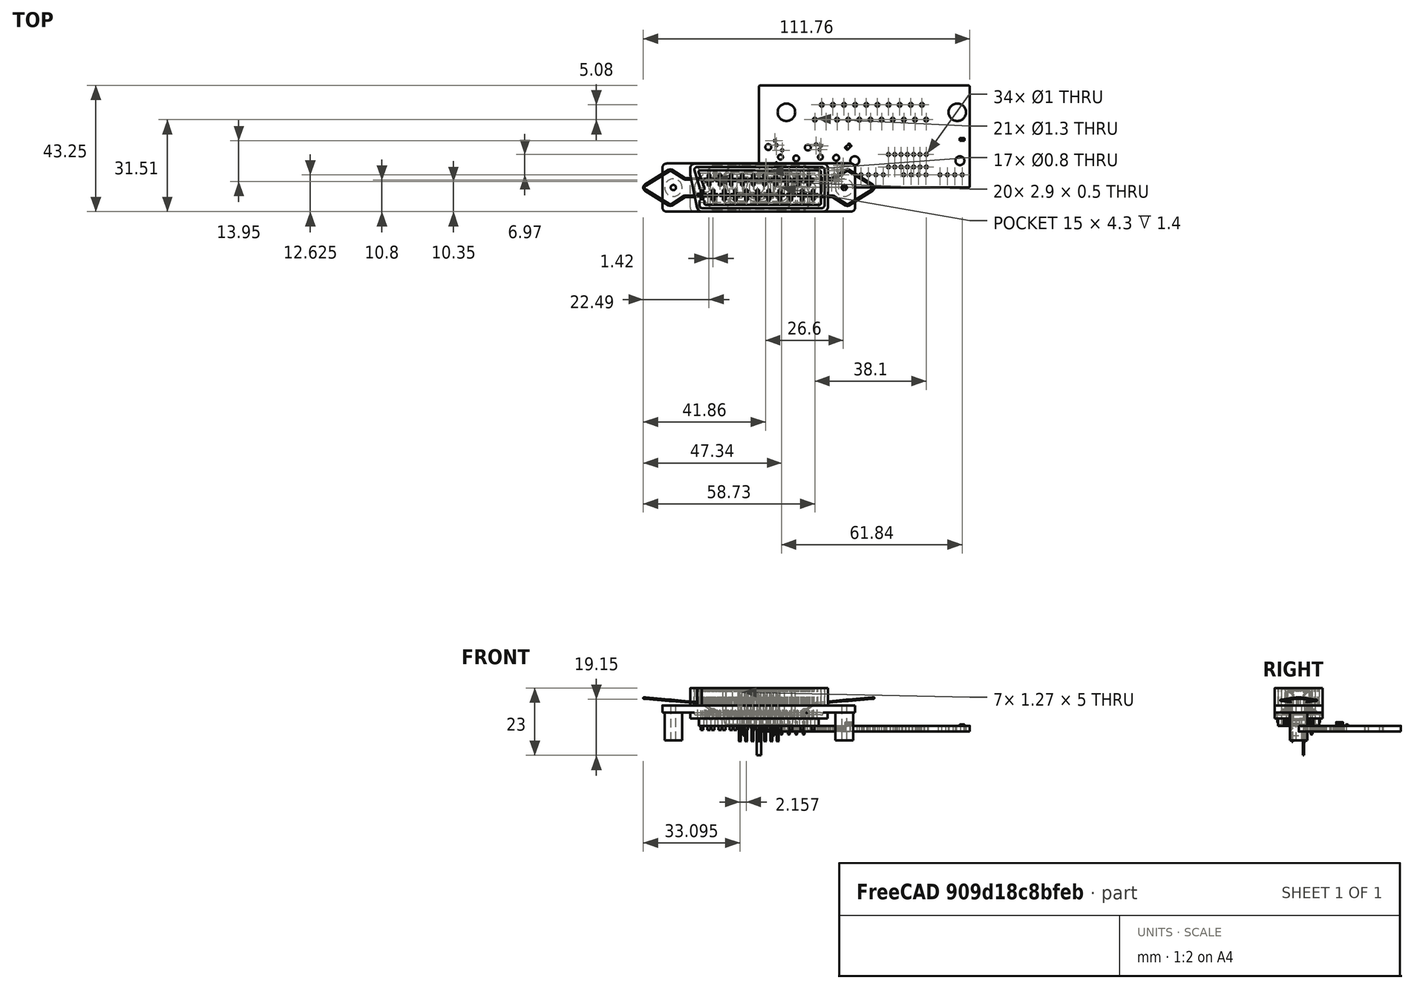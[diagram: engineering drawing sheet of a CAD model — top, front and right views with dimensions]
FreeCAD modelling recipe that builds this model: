
FCSTD DOCUMENT  (FreeCAD 0.20R29177 (Git))
Label: Ultra-AV
License: All rights reserved
LicenseURL: http://en.wikipedia.org/wiki/All_rights_reserved
objects: Part::Feature×44, App::Part×14, App::Link×9, PartDesign::AdditiveBox×8, PartDesign::AdditiveCylinder×6, PartDesign::SubtractiveCylinder×4, PartDesign::Body×4, PartDesign::Fillet×4, Sketcher::SketchObject×3, PartDesign::CoordinateSystem×1
note: 96 computed .brp shape members not serialized (recipe doc carries the construction recipe); baked Part::Feature solids carry a one-line shape summary decoded from their .brp

FEATURE [PartDesign::CoordinateSystem] Local_CS_ecc4
  AttacherType = Attacher::AttachEngine3D
FEATURE [Part::Feature] Pcb_ecc4
  Placement = pos=(-111.2,111.3,0) rot=(0,0,1;0rad)
  shape: bbox 72.2 x 35 x 2 mm, 96 faces (baked)
FEATURE [Sketcher::SketchObject] PCB_Sketch_ecc4
  FullyConstrained = false
  sketch-geometry (29):
    g0: LineSegment StartX=0.5 StartY=35 StartZ=0 EndX=71.7 EndY=35 EndZ=0
    g1: LineSegment StartX=0.001685 StartY=7.99999 StartZ=0 EndX=3e-16 EndY=34.5 EndZ=0
    g2: LineSegment StartX=72.2 StartY=34.5 StartZ=0 EndX=72.2 EndY=0.5 EndZ=0
    g3: LineSegment StartX=71.7 StartY=2.8e-15 StartZ=0 EndX=8.00168 EndY=-7e-06 EndZ=0
    g4: ArcOfCircle CenterX=8.00169 CenterY=7.99999 CenterZ=0 NormalX=0 NormalY=0 NormalZ=-1 AngleXU=-1.5708 Radius=8 StartAngle=0 EndAngle=1.5708
    g5: ArcOfCircle CenterX=0.500001 CenterY=34.5 CenterZ=0 NormalX=0 NormalY=0 NormalZ=-1 AngleXU=2.66714e-06 Radius=0.500001 StartAngle=0 EndAngle=1.57079
    g6: ArcOfCircle CenterX=71.7 CenterY=34.5 CenterZ=0 NormalX=0 NormalY=0 NormalZ=-1 AngleXU=1.5708 Radius=0.500001 StartAngle=0 EndAngle=1.57079
    g7: ArcOfCircle CenterX=71.7 CenterY=0.500001 CenterZ=0 NormalX=0 NormalY=0 NormalZ=-1 AngleXU=-3.14159 Radius=0.500001 StartAngle=0 EndAngle=1.57079
    g8: Circle CenterX=26.9 CenterY=5.8 CenterZ=0 NormalX=0 NormalY=0 NormalZ=1 AngleXU=0 Radius=0.4
    g9: Circle CenterX=28.9 CenterY=7.6 CenterZ=0 NormalX=0 NormalY=0 NormalZ=1 AngleXU=0 Radius=0.4
    g10: Circle CenterX=11.8 CenterY=2.95 CenterZ=0 NormalX=0 NormalY=0 NormalZ=1 AngleXU=0 Radius=0.25
    g11: Circle CenterX=19.6 CenterY=14.8 CenterZ=0 NormalX=0 NormalY=0 NormalZ=1 AngleXU=0 Radius=0.4
    g12: Circle CenterX=6 CenterY=8.4 CenterZ=0 NormalX=0 NormalY=0 NormalZ=1 AngleXU=0 Radius=0.25
    g13: Circle CenterX=6.05 CenterY=14.55 CenterZ=0 NormalX=0 NormalY=0 NormalZ=1 AngleXU=0 Radius=0.4
    g14: Circle CenterX=23.5 CenterY=2.1 CenterZ=0 NormalX=0 NormalY=0 NormalZ=1 AngleXU=0 Radius=0.4
    g15: Circle CenterX=28.2 CenterY=6.3 CenterZ=0 NormalX=0 NormalY=0 NormalZ=1 AngleXU=0 Radius=0.4
    g16: Circle CenterX=22.2 CenterY=2.1 CenterZ=0 NormalX=0 NormalY=0 NormalZ=1 AngleXU=0 Radius=0.4
    g17: Circle CenterX=2.5 CenterY=7.4 CenterZ=0 NormalX=0 NormalY=0 NormalZ=1 AngleXU=0 Radius=0.4
    g18: Circle CenterX=3.1 CenterY=5 CenterZ=0 NormalX=0 NormalY=0 NormalZ=1 AngleXU=0 Radius=0.4
    g19: Circle CenterX=27.4 CenterY=2.8 CenterZ=0 NormalX=0 NormalY=0 NormalZ=1 AngleXU=0 Radius=0.4
    g20: Circle CenterX=20.8 CenterY=13 CenterZ=0 NormalX=0 NormalY=0 NormalZ=1 AngleXU=0 Radius=0.4
    g21: Circle CenterX=21.2 CenterY=14.3 CenterZ=0 NormalX=0 NormalY=0 NormalZ=1 AngleXU=0 Radius=0.4
    g22: Circle CenterX=4.55 CenterY=6 CenterZ=0 NormalX=0 NormalY=0 NormalZ=1 AngleXU=0 Radius=0.25
    g23: Circle CenterX=8 CenterY=12.8 CenterZ=0 NormalX=0 NormalY=0 NormalZ=1 AngleXU=0 Radius=0.4
    g24: Circle CenterX=10.9 CenterY=2.75 CenterZ=0 NormalX=0 NormalY=0 NormalZ=1 AngleXU=0 Radius=0.25
    g25: Circle CenterX=26.3 CenterY=2.1 CenterZ=0 NormalX=0 NormalY=0 NormalZ=1 AngleXU=0 Radius=0.4
    g26: Circle CenterX=24.9 CenterY=2.1 CenterZ=0 NormalX=0 NormalY=0 NormalZ=1 AngleXU=0 Radius=0.4
    g27: Circle CenterX=5.55 CenterY=16.05 CenterZ=0 NormalX=0 NormalY=0 NormalZ=1 AngleXU=0 Radius=0.4
    g28: Circle CenterX=2.3 CenterY=6.1 CenterZ=0 NormalX=0 NormalY=0 NormalZ=1 AngleXU=0 Radius=0.4
  constraints (8):
    c: Coincident(g1,g4)
    c: Coincident(g1,g5)
    c: Coincident(g0,g5)
    c: Coincident(g3,g4)
    c: Coincident(g3,g7)
    c: Coincident(g0,g6)
    c: Coincident(g2,g7)
    c: Coincident(g2,g6)
FEATURE [App::Part] Board_Geoms_ecc4
  Group = -> [Local_CS_ecc4,Pcb_ecc4,PCB_Sketch_ecc4]
  Origin = -> Origin
FEATURE [Part::Feature] Shape  label="R12_R_0603_1608Metric_fea975d0d3e0"
  Placement = pos=(69.6,16.5,0) rot=(0,0,1;0rad)
  shape: bbox 1.6 x 0.8 x 0.45 mm, 26 faces (baked)
FEATURE [Part::Feature] Shape001  label="J5_PinHeader_1x04_P254mm_Horizontal_92fba9bb2b89"
  Placement = pos=(15.4,4.4,0) rot=(0,0,-1;1.5708rad)
  shape: bbox 10.16 x 10.36 x 5.54 mm, 112 faces (baked)
FEATURE [App::Link] R12_R_0603_1608Metric_fea975d0d3e0_ln_  label="R16_R_0603_1608Metric_98c7d70c461d"
  LinkPlacement = pos=(70.45,14.175,0) rot=(0,0,-1;0.785398rad)
  LinkedObject = -> Shape
  Placement = pos=(70.45,14.175,0) rot=(0,0,-1;0.785398rad)
FEATURE [Part::Feature] Part__Feature  label="Plastic-insert"
  Placement = pos=(0,0,0.05) rot=(0,0,1;0rad)
  shape: bbox 22.57 x 11.5 x 12.3 mm, 343 faces (baked)
FEATURE [Part::Feature] Part__Feature001  label="chassis-metal"
  Placement = pos=(0,0,4.5) rot=(0,0,1;0rad)
  shape: bbox 43.9 x 15.3 x 12.3 mm, 159 faces (baked)
FEATURE [Part::Feature] Part__Feature002  label="base-pin"
  Placement = pos=(-6.48,0,4.5) rot=(0,0,1;0rad)
  shape: bbox 1.5 x 1.495 x 17.96 mm, 46 faces (baked)
FEATURE [Part::Feature] Part__Feature003  label="base-pin001"
  Placement = pos=(-4.32,0,4.5) rot=(0,0,1;0rad)
  shape: bbox 1.5 x 1.495 x 17.96 mm, 46 faces (baked)
FEATURE [Part::Feature] Part__Feature004  label="base-pin002"
  Placement = pos=(-2.16,0,4.5) rot=(0,0,1;0rad)
  shape: bbox 1.5 x 1.495 x 17.96 mm, 46 faces (baked)
FEATURE [Part::Feature] Part__Feature005  label="base-pin003"
  Placement = pos=(0,0,4.5) rot=(0,0,1;0rad)
  shape: bbox 1.5 x 1.495 x 17.96 mm, 46 faces (baked)
FEATURE [Part::Feature] Part__Feature006  label="base-pin004"
  Placement = pos=(2.16,0,4.5) rot=(0,0,1;0rad)
  shape: bbox 1.5 x 1.495 x 17.96 mm, 46 faces (baked)
FEATURE [Part::Feature] Part__Feature007  label="base-pin005"
  Placement = pos=(4.32,0,4.5) rot=(0,0,1;0rad)
  shape: bbox 1.5 x 1.495 x 17.96 mm, 46 faces (baked)
FEATURE [Part::Feature] Part__Feature008  label="base-pin006"
  Placement = pos=(6.48,0,4.5) rot=(0,0,1;0rad)
  shape: bbox 1.5 x 1.495 x 17.96 mm, 46 faces (baked)
FEATURE [App::Part] pins_top  label="pins-top"
  Group = -> [Part__Feature002,Part__Feature003,Part__Feature004,Part__Feature005,Part__Feature006,Part__Feature007,Part__Feature008]
  Origin = -> Origin008
FEATURE [Part::Feature] Part__Feature009  label="pins-bot"
  Placement = pos=(0,0,0) rot=(0,0,1;3.14159rad)
  shape: bbox 1.5 x 1.495 x 17.96 mm, 46 faces (baked)
FEATURE [Part::Feature] Part__Feature010  label="pins-bot001"
  Placement = pos=(0,0,0) rot=(0,0,1;3.14159rad)
  shape: bbox 1.5 x 1.495 x 17.96 mm, 46 faces (baked)
FEATURE [Part::Feature] Part__Feature011  label="pins-bot002"
  Placement = pos=(0,0,0) rot=(0,0,1;3.14159rad)
  shape: bbox 1.5 x 1.495 x 17.96 mm, 46 faces (baked)
FEATURE [Part::Feature] Part__Feature012  label="pins-bot003"
  Placement = pos=(0,0,0) rot=(0,0,1;3.14159rad)
  shape: bbox 1.5 x 1.495 x 17.96 mm, 46 faces (baked)
FEATURE [Part::Feature] Part__Feature013  label="pins-bot004"
  Placement = pos=(0,0,0) rot=(0,0,1;3.14159rad)
  shape: bbox 1.5 x 1.495 x 17.96 mm, 46 faces (baked)
FEATURE [Part::Feature] Part__Feature014  label="pins-bot005"
  Placement = pos=(0,0,0) rot=(0,0,1;3.14159rad)
  shape: bbox 1.5 x 1.495 x 17.96 mm, 46 faces (baked)
FEATURE [Part::Feature] Part__Feature015  label="pins-bot006"
  Placement = pos=(0,0,0) rot=(0,0,1;3.14159rad)
  shape: bbox 1.5 x 1.495 x 17.96 mm, 46 faces (baked)
FEATURE [App::Part] pins_bot  label="pins-bot007"
  Group = -> [Part__Feature009,Part__Feature010,Part__Feature011,Part__Feature012,Part__Feature013,Part__Feature014,Part__Feature015]
  Origin = -> Origin009
FEATURE [Part::Feature] Part__Feature017  label="Handle Left"
  shape: bbox 24.46 x 12.5 x 5.12 mm, 52 faces (baked)
FEATURE [Part::Feature] Part__Feature018  label="Handle Right"
  Placement = pos=(0,0,0) rot=(0,0,1;3.14159rad)
  shape: bbox 24.46 x 12.5 x 5.12 mm, 52 faces (baked)
FEATURE [App::Part] Handles
  Group = -> [Part__Feature017,Part__Feature018]
  Origin = -> Origin010
FEATURE [App::Part] Norcomp_111_014_213L001  label="J9_Norcomp_111_014_213L001_9b66603eb921"
  Group = -> [Part__Feature,Part__Feature001,pins_top,pins_bot,Handles]
  Origin = -> Origin011
  Placement = pos=(50.85,9.2,0) rot=(0,0,1;0rad)
FEATURE [App::Link] J5_PinHeader_1x04_P254mm_Horizontal_92fba9bb2b89_ln_  label="J3_PinHeader_1x04_P254mm_Horizontal_ad84bd842bec"
  LinkPlacement = pos=(28.4,4.4,0) rot=(0,0,-1;1.5708rad)
  LinkedObject = -> Shape001
  Placement = pos=(28.4,4.4,0) rot=(0,0,-1;1.5708rad)
FEATURE [App::Link] R12_R_0603_1608Metric_fea975d0d3e0_ln_001  label="R100_R_0603_1608Metric_c06db4a17feb"
  LinkPlacement = pos=(29.3664,15.2664,0) rot=(0,0,1;3.92699rad)
  LinkedObject = -> Shape
  Placement = pos=(29.3664,15.2664,0) rot=(0,0,1;3.92699rad)
FEATURE [Part::Feature] Part__Feature019  label="Plastic-body"
  Placement = pos=(0,0,7) rot=(0,0,1;0rad)
  shape: bbox 66 x 16.5 x 17.9 mm, 446 faces (baked)
FEATURE [Part::Feature] Part__Feature020  label="pin-top"
  Placement = pos=(2.38,5.0875,0) rot=(0,0,1;0rad)
  shape: bbox 2.8 x 0.4 x 14.4 mm, 20 faces (baked)
FEATURE [Part::Feature] Part__Feature021  label="pin-top001"
  Placement = pos=(6.18,5.0875,0) rot=(0,0,1;0rad)
  shape: bbox 2.8 x 0.4 x 14.4 mm, 20 faces (baked)
FEATURE [Part::Feature] Part__Feature022  label="pin-top002"
  Placement = pos=(9.98,5.0875,0) rot=(0,0,1;0rad)
  shape: bbox 2.8 x 0.4 x 14.4 mm, 20 faces (baked)
FEATURE [Part::Feature] Part__Feature023  label="pin-top003"
  Placement = pos=(13.78,5.0875,0) rot=(0,0,1;0rad)
  shape: bbox 2.8 x 0.4 x 14.4 mm, 20 faces (baked)
FEATURE [Part::Feature] Part__Feature024  label="pin-top004"
  Placement = pos=(17.58,5.0875,0) rot=(0,0,1;0rad)
  shape: bbox 2.8 x 0.4 x 14.4 mm, 20 faces (baked)
FEATURE [Part::Feature] Part__Feature025  label="pin-top005"
  Placement = pos=(21.38,5.0875,0) rot=(0,0,1;0rad)
  shape: bbox 2.8 x 0.4 x 14.4 mm, 20 faces (baked)
FEATURE [Part::Feature] Part__Feature026  label="pin-top006"
  Placement = pos=(25.18,5.0875,0) rot=(0,0,1;0rad)
  shape: bbox 2.8 x 0.4 x 14.4 mm, 20 faces (baked)
FEATURE [Part::Feature] Part__Feature027  label="pin-top007"
  Placement = pos=(28.98,5.0875,0) rot=(0,0,1;0rad)
  shape: bbox 2.8 x 0.4 x 14.4 mm, 20 faces (baked)
FEATURE [Part::Feature] Part__Feature028  label="pin-top008"
  Placement = pos=(32.78,5.0875,0) rot=(0,0,1;0rad)
  shape: bbox 2.8 x 0.4 x 14.4 mm, 20 faces (baked)
FEATURE [Part::Feature] Part__Feature029  label="pin-top009"
  Placement = pos=(36.58,5.0875,0) rot=(0,0,1;0rad)
  shape: bbox 2.8 x 0.4 x 14.4 mm, 20 faces (baked)
FEATURE [App::Part] top_pins  label="top-pins"
  Group = -> [Part__Feature020,Part__Feature021,Part__Feature022,Part__Feature023,Part__Feature024,Part__Feature025,Part__Feature026,Part__Feature027,Part__Feature028,Part__Feature029]
  Origin = -> Origin012
FEATURE [Part::Feature] Part__Feature030  label="Pin-bot"
  shape: bbox 2.8 x 0.4 x 14.4 mm, 20 faces (baked)
FEATURE [Part::Feature] Part__Feature031  label="Pin-bot001"
  Placement = pos=(3.8,0,0) rot=(0,0,1;0rad)
  shape: bbox 2.8 x 0.4 x 14.4 mm, 20 faces (baked)
FEATURE [Part::Feature] Part__Feature032  label="Pin-bot002"
  Placement = pos=(7.6,0,0) rot=(0,0,1;0rad)
  shape: bbox 2.8 x 0.4 x 14.4 mm, 20 faces (baked)
FEATURE [Part::Feature] Part__Feature033  label="Pin-bot003"
  Placement = pos=(11.4,0,0) rot=(0,0,1;0rad)
  shape: bbox 2.8 x 0.4 x 14.4 mm, 20 faces (baked)
FEATURE [Part::Feature] Part__Feature034  label="Pin-bot004"
  Placement = pos=(15.2,0,0) rot=(0,0,1;0rad)
  shape: bbox 2.8 x 0.4 x 14.4 mm, 20 faces (baked)
FEATURE [Part::Feature] Part__Feature035  label="Pin-bot005"
  Placement = pos=(19,0,0) rot=(0,0,1;0rad)
  shape: bbox 2.8 x 0.4 x 14.4 mm, 20 faces (baked)
FEATURE [Part::Feature] Part__Feature036  label="Pin-bot006"
  Placement = pos=(22.8,0,0) rot=(0,0,1;0rad)
  shape: bbox 2.8 x 0.4 x 14.4 mm, 20 faces (baked)
FEATURE [Part::Feature] Part__Feature037  label="Pin-bot007"
  Placement = pos=(26.6,0,0) rot=(0,0,1;0rad)
  shape: bbox 2.8 x 0.4 x 14.4 mm, 20 faces (baked)
FEATURE [Part::Feature] Part__Feature038  label="Pin-bot008"
  Placement = pos=(30.4,0,0) rot=(0,0,1;0rad)
  shape: bbox 2.8 x 0.4 x 14.4 mm, 20 faces (baked)
FEATURE [Part::Feature] Part__Feature039  label="Pin-bot009"
  Placement = pos=(34.2,0,0) rot=(0,0,1;0rad)
  shape: bbox 2.8 x 0.4 x 14.4 mm, 20 faces (baked)
FEATURE [Part::Feature] Part__Feature040  label="Pin-bot010"
  Placement = pos=(38,0,0) rot=(0,0,1;0rad)
  shape: bbox 2.8 x 0.4 x 14.4 mm, 20 faces (baked)
FEATURE [App::Part] Array001
  Group = -> [Part__Feature030,Part__Feature031,Part__Feature032,Part__Feature033,Part__Feature034,Part__Feature035,Part__Feature036,Part__Feature037,Part__Feature038,Part__Feature039,Part__Feature040]
  Origin = -> Origin013
FEATURE [App::Part] TC_1578891_scart  label="J11_TC_1578891_scart_58c3af9e474b"
  Group = -> [Part__Feature019,top_pins,Array001]
  Origin = -> Origin014
  Placement = pos=(38.7,25.8,0) rot=(0,0,1;0rad)
FEATURE [Part::Feature] Shape002  label="C100_C_0805_2012Metric_50f9677266a3"
  Placement = pos=(30.6,14,0) rot=(0,0,1;0.785398rad)
  shape: bbox 2.298 x 2.298 x 1.25 mm, 28 faces (baked)
FEATURE [App::Link] R12_R_0603_1608Metric_fea975d0d3e0_ln_002  label="R17_R_0603_1608Metric_099708a927e8"
  LinkPlacement = pos=(32.6166,2.78336,0) rot=(0,0,-1;0.785398rad)
  LinkedObject = -> Shape
  Placement = pos=(32.6166,2.78336,0) rot=(0,0,-1;0.785398rad)
FEATURE [App::Link] J5_PinHeader_1x04_P254mm_Horizontal_92fba9bb2b89_ln_001  label="J1_PinHeader_1x04_P254mm_Horizontal_e9d8d5db6f15"
  LinkPlacement = pos=(62,4.375,-2) rot=(0.707107,-0.707107,0;3.14159rad)
  LinkedObject = -> Shape001
  Placement = pos=(62,4.375,-2) rot=(0.707107,-0.707107,0;3.14159rad)
FEATURE [App::Link] R12_R_0603_1608Metric_fea975d0d3e0_ln_003  label="R2_R_0603_1608Metric_0536453e6189"
  LinkPlacement = pos=(23.8,12.8,-2) rot=(0,1,0;3.14159rad)
  LinkedObject = -> Shape
  Placement = pos=(23.8,12.8,-2) rot=(0,1,0;3.14159rad)
FEATURE [App::Link] J5_PinHeader_1x04_P254mm_Horizontal_92fba9bb2b89_ln_002  label="J4_PinHeader_1x04_P254mm_Horizontal_ed954c910011"
  LinkPlacement = pos=(35,4.4,-2) rot=(0.707107,-0.707107,0;3.14159rad)
  LinkedObject = -> Shape001
  Placement = pos=(35,4.4,-2) rot=(0.707107,-0.707107,0;3.14159rad)
FEATURE [App::Link] R12_R_0603_1608Metric_fea975d0d3e0_ln_004  label="R1_R_0603_1608Metric_fdd1dcc8b35c"
  LinkPlacement = pos=(17.6334,10.3834,-2) rot=(0.92388,0.382683,0;3.14159rad)
  LinkedObject = -> Shape
  Placement = pos=(17.6334,10.3834,-2) rot=(0.92388,0.382683,0;3.14159rad)
FEATURE [App::Link] J5_PinHeader_1x04_P254mm_Horizontal_92fba9bb2b89_ln_003  label="J2_PinHeader_1x04_P254mm_Horizontal_2a461bf643cc"
  LinkPlacement = pos=(49.6,4.4,-2) rot=(0.707107,-0.707107,0;3.14159rad)
  LinkedObject = -> Shape001
  Placement = pos=(49.6,4.4,-2) rot=(0.707107,-0.707107,0;3.14159rad)
FEATURE [App::Part] Bot_ecc4
  Group = -> [J5_PinHeader_1x04_P254mm_Horizontal_92fba9bb2b89_ln_001,R12_R_0603_1608Metric_fea975d0d3e0_ln_003,J5_PinHeader_1x04_P254mm_Horizontal_92fba9bb2b89_ln_002,R12_R_0603_1608Metric_fea975d0d3e0_ln_004,J5_PinHeader_1x04_P254mm_Horizontal_92fba9bb2b89_ln_003]
  Origin = -> Origin004
FEATURE [PartDesign::AdditiveBox] Box
  AttacherType = Attacher::AttachEngine3D
  AttachmentOffset = pos=(-5.35,-3,0) rot=(0,0,1;0rad)
  Height = 0.4
  Length = 10.7
  MapMode = 5
  Placement = pos=(-5.35,-3,0) rot=(0,0,1;0rad)
  Support = -> [XY_Plane015]
  Width = 6
FEATURE [PartDesign::AdditiveCylinder] Cylinder
  Angle = 360
  AttacherType = Attacher::AttachEngine3D
  BaseFeature = -> Box
  FirstAngle = 0
  Height = 0.4
  MapMode = 5
  Radius = 5
  SecondAngle = 0
  Support = -> [XY_Plane015]
FEATURE [PartDesign::AdditiveCylinder] Cylinder001
  Angle = 360
  AttacherType = Attacher::AttachEngine3D
  BaseFeature = -> Cylinder
  FirstAngle = 0
  Height = 12
  MapMode = 5
  Radius = 4.15
  SecondAngle = 0
  Support = -> [XY_Plane015]
FEATURE [PartDesign::AdditiveCylinder] Cylinder003
  Angle = 360
  AttacherType = Attacher::AttachEngine3D
  AttachmentOffset = pos=(0,0,2) rot=(0,0,1;0rad)
  FirstAngle = 0
  Height = 10
  MapMode = 5
  Placement = pos=(0,0,2) rot=(0,0,1;0rad)
  Radius = 3.27
  SecondAngle = 0
  Support = -> [XY_Plane016]
FEATURE [PartDesign::SubtractiveCylinder] Cylinder004
  Angle = 360
  AttacherType = Attacher::AttachEngine3D
  AttachmentOffset = pos=(0,0,2) rot=(0,0,1;0rad)
  BaseFeature = -> Cylinder003
  FirstAngle = 0
  Height = 10
  MapMode = 5
  Placement = pos=(0,0,2) rot=(0,0,1;0rad)
  Radius = 1.75
  SecondAngle = 0
  Support = -> [XY_Plane016]
FEATURE [PartDesign::Body] Body001  label="Red inset"
  Group = -> [Cylinder003,Cylinder004]
  Origin = -> Origin016
  Tip = -> Cylinder004
FEATURE [PartDesign::Fillet] Fillet
  Base = -> Cylinder001 [Edge37]
  BaseFeature = -> Cylinder001
  Radius = 0.75
  SupportTransform = false
  UseAllEdges = false
FEATURE [PartDesign::SubtractiveCylinder] Cylinder002
  Angle = 360
  AttacherType = Attacher::AttachEngine3D
  AttachmentOffset = pos=(0,0,2) rot=(0,0,1;0rad)
  BaseFeature = -> Fillet
  FirstAngle = 0
  Height = 10
  MapMode = 5
  Placement = pos=(0,0,2) rot=(0,0,1;0rad)
  Radius = 3.3
  SecondAngle = 0
  Support = -> [XY_Plane015]
FEATURE [PartDesign::Fillet] Fillet001
  Base = -> Cylinder002 [Edge19]
  BaseFeature = -> Cylinder002
  Placement = pos=(0,0,2) rot=(0,0,1;0rad)
  Radius = 0.2
  SupportTransform = false
  UseAllEdges = false
FEATURE [PartDesign::AdditiveBox] Box001
  AttacherType = Attacher::AttachEngine3D
  AttachmentOffset = pos=(-0.75,1.4,-10.1) rot=(0,0,1;0rad)
  BaseFeature = -> Fillet001
  Height = 10.1
  Length = 1.5
  MapMode = 5
  Placement = pos=(-0.75,1.4,-10.1) rot=(0,0,1;0rad)
  Support = -> [XY_Plane015]
  Width = 0.4
FEATURE [PartDesign::AdditiveBox] Box002
  AttacherType = Attacher::AttachEngine3D
  AttachmentOffset = pos=(4.95,-3,-3.4) rot=(0,0,1;0rad)
  BaseFeature = -> Box001
  Height = 3.8
  Length = 0.4
  MapMode = 5
  Placement = pos=(4.95,-3,-3.4) rot=(0,0,1;0rad)
  Support = -> [XY_Plane015]
  Width = 6
FEATURE [PartDesign::AdditiveBox] Box003
  AttacherType = Attacher::AttachEngine3D
  AttachmentOffset = pos=(-5.35,-3,-3.4) rot=(0,0,1;0rad)
  BaseFeature = -> Box002
  Height = 3.8
  Length = 0.4
  MapMode = 5
  Placement = pos=(-5.35,-3,-3.4) rot=(0,0,1;0rad)
  Support = -> [XY_Plane015]
  Width = 6
FEATURE [Sketcher::SketchObject] Sketch  label="chassis-sketch"
  FullyConstrained = false
  MapMode = 5
  Support = -> [XY_Plane015]
  sketch-geometry (36):
    g0: ArcOfCircle CenterX=0 CenterY=0 CenterZ=0 NormalX=0 NormalY=0 NormalZ=1 AngleXU=0 Radius=5.05 StartAngle=5.65934 EndAngle=6.28319
    g1: ArcOfCircle CenterX=0 CenterY=0 CenterZ=0 NormalX=0 NormalY=0 NormalZ=1 AngleXU=0 Radius=5.05 StartAngle=0 EndAngle=0.623843
    g2: ArcOfCircle CenterX=0 CenterY=0 CenterZ=0 NormalX=0 NormalY=0 NormalZ=1 AngleXU=0 Radius=5.05 StartAngle=0.648461 EndAngle=2.49313
    g3: ArcOfCircle CenterX=0 CenterY=0 CenterZ=0 NormalX=0 NormalY=0 NormalZ=1 AngleXU=0 Radius=5.05 StartAngle=2.51775 EndAngle=3.76544
    g4: ArcOfCircle CenterX=0 CenterY=0 CenterZ=0 NormalX=0 NormalY=0 NormalZ=1 AngleXU=0 Radius=5.05 StartAngle=3.79005 EndAngle=5.63472
    g5: ArcOfCircle CenterX=0 CenterY=0 CenterZ=0 NormalX=0 NormalY=0 NormalZ=1 AngleXU=0 Radius=4.95 StartAngle=5.6397 EndAngle=6.28319
    g6: ArcOfCircle CenterX=0 CenterY=0 CenterZ=0 NormalX=0 NormalY=0 NormalZ=1 AngleXU=0 Radius=4.95 StartAngle=0 EndAngle=0.643481
    g7: ArcOfCircle CenterX=0 CenterY=0 CenterZ=0 NormalX=0 NormalY=0 NormalZ=1 AngleXU=0 Radius=4.95 StartAngle=0.643521 EndAngle=2.49807
    g8: ArcOfCircle CenterX=0 CenterY=0 CenterZ=0 NormalX=0 NormalY=0 NormalZ=1 AngleXU=0 Radius=4.95 StartAngle=2.49811 EndAngle=3.78507
    g9: ArcOfCircle CenterX=0 CenterY=0 CenterZ=0 NormalX=0 NormalY=0 NormalZ=1 AngleXU=0 Radius=4.95 StartAngle=3.78511 EndAngle=5.63966
    g10: Circle CenterX=0 CenterY=0 CenterZ=0 NormalX=0 NormalY=0 NormalZ=1 AngleXU=0 Radius=1.3
    g11: Circle CenterX=0 CenterY=0 CenterZ=0 NormalX=0 NormalY=0 NormalZ=1 AngleXU=0 Radius=1.2
    g12: LineSegment StartX=-5.4 StartY=-3 StartZ=0 EndX=-5.4 EndY=3 EndZ=0
    g13: ArcOfCircle CenterX=-5.35 CenterY=3 CenterZ=0 NormalX=0 NormalY=0 NormalZ=1 AngleXU=-1e-16 Radius=0.05 StartAngle=0 EndAngle=3.14159
    g14: LineSegment StartX=-5.3 StartY=3 StartZ=0 EndX=-5.3 EndY=-3 EndZ=0
    g15: ArcOfCircle CenterX=-5.35 CenterY=-3 CenterZ=0 NormalX=0 NormalY=0 NormalZ=1 AngleXU=-1e-16 Radius=0.05 StartAngle=3.14159 EndAngle=6.28319
    g16: LineSegment StartX=5.3 StartY=-3 StartZ=0 EndX=5.3 EndY=3 EndZ=0
    g17: ArcOfCircle CenterX=5.35 CenterY=3 CenterZ=0 NormalX=0 NormalY=0 NormalZ=1 AngleXU=-1e-16 Radius=0.05 StartAngle=0 EndAngle=3.14159
    g18: LineSegment StartX=5.4 StartY=3 StartZ=0 EndX=5.4 EndY=-3 EndZ=0
    g19: ArcOfCircle CenterX=5.35 CenterY=-3 CenterZ=0 NormalX=0 NormalY=0 NormalZ=1 AngleXU=-1e-16 Radius=0.05 StartAngle=3.14159 EndAngle=6.28319
    g20: LineSegment StartX=-4 StartY=-3.05 StartZ=0 EndX=-5.35 EndY=-3.05 EndZ=0
    g21: ArcOfCircle CenterX=-5.35 CenterY=-3 CenterZ=0 NormalX=0 NormalY=0 NormalZ=1 AngleXU=1.5708 Radius=0.05 StartAngle=0 EndAngle=3.14159
    g22: LineSegment StartX=-5.35 StartY=-2.95 StartZ=0 EndX=-4 EndY=-2.95 EndZ=0
    g23: ArcOfCircle CenterX=-4 CenterY=-3 CenterZ=0 NormalX=0 NormalY=0 NormalZ=1 AngleXU=1.5708 Radius=0.05 StartAngle=3.14159 EndAngle=6.28319
    g24: LineSegment StartX=5.35 StartY=-3.05 StartZ=0 EndX=4 EndY=-3.05 EndZ=0
    g25: ArcOfCircle CenterX=4 CenterY=-3 CenterZ=0 NormalX=0 NormalY=0 NormalZ=1 AngleXU=1.5708 Radius=0.05 StartAngle=0 EndAngle=3.14159
    g26: LineSegment StartX=4 StartY=-2.95 StartZ=0 EndX=5.35 EndY=-2.95 EndZ=0
    g27: ArcOfCircle CenterX=5.35 CenterY=-3 CenterZ=0 NormalX=0 NormalY=0 NormalZ=1 AngleXU=1.5708 Radius=0.05 StartAngle=3.14159 EndAngle=6.28319
    g28: LineSegment StartX=5.35 StartY=2.95 StartZ=0 EndX=4 EndY=2.95 EndZ=0
    g29: ArcOfCircle CenterX=4 CenterY=3 CenterZ=0 NormalX=0 NormalY=0 NormalZ=1 AngleXU=1.5708 Radius=0.05 StartAngle=0 EndAngle=3.14159
    g30: LineSegment StartX=4 StartY=3.05 StartZ=0 EndX=5.35 EndY=3.05 EndZ=0
    g31: ArcOfCircle CenterX=5.35 CenterY=3 CenterZ=0 NormalX=0 NormalY=0 NormalZ=1 AngleXU=1.5708 Radius=0.05 StartAngle=3.14159 EndAngle=6.28319
    g32: LineSegment StartX=-4 StartY=2.95 StartZ=0 EndX=-5.35 EndY=2.95 EndZ=0
    g33: ArcOfCircle CenterX=-5.35 CenterY=3 CenterZ=0 NormalX=0 NormalY=0 NormalZ=1 AngleXU=1.5708 Radius=0.05 StartAngle=0 EndAngle=3.14159
    g34: LineSegment StartX=-5.35 StartY=3.05 StartZ=0 EndX=-4 EndY=3.05 EndZ=0
    g35: ArcOfCircle CenterX=-4 CenterY=3 CenterZ=0 NormalX=0 NormalY=0 NormalZ=1 AngleXU=1.5708 Radius=0.05 StartAngle=3.14159 EndAngle=6.28319
FEATURE [PartDesign::Body] Body
  Group = -> [Sketch,Box,Cylinder,Cylinder001,Fillet,Cylinder002,Fillet001,Box001,Box002,Box003]
  Origin = -> Origin015
  Tip = -> Box003
FEATURE [App::Part] Part  label="RCA-RED"
  Group = -> [Body,Body001]
  Origin = -> Origin017
  Placement = pos=(8.05,12,4) rot=(0,0,1;2.75762rad)
FEATURE [PartDesign::AdditiveBox] Box004
  AttacherType = Attacher::AttachEngine3D
  AttachmentOffset = pos=(-5.35,-3,0) rot=(0,0,1;0rad)
  Height = 0.4
  Length = 10.7
  MapMode = 5
  Placement = pos=(-5.35,-3,0) rot=(0,0,1;0rad)
  Support = -> [XY_Plane018]
  Width = 6
FEATURE [PartDesign::AdditiveCylinder] Cylinder005
  Angle = 360
  AttacherType = Attacher::AttachEngine3D
  BaseFeature = -> Box004
  FirstAngle = 0
  Height = 0.4
  MapMode = 5
  Radius = 5
  SecondAngle = 0
  Support = -> [XY_Plane018]
FEATURE [PartDesign::AdditiveCylinder] Cylinder006
  Angle = 360
  AttacherType = Attacher::AttachEngine3D
  BaseFeature = -> Cylinder005
  FirstAngle = 0
  Height = 12
  MapMode = 5
  Radius = 4.15
  SecondAngle = 0
  Support = -> [XY_Plane018]
FEATURE [PartDesign::AdditiveCylinder] Cylinder008
  Angle = 360
  AttacherType = Attacher::AttachEngine3D
  AttachmentOffset = pos=(0,0,2) rot=(0,0,1;0rad)
  FirstAngle = 0
  Height = 10
  MapMode = 5
  Placement = pos=(0,0,2) rot=(0,0,1;0rad)
  Radius = 3.27
  SecondAngle = 0
  Support = -> [XY_Plane019]
FEATURE [PartDesign::SubtractiveCylinder] Cylinder009
  Angle = 360
  AttacherType = Attacher::AttachEngine3D
  AttachmentOffset = pos=(0,0,2) rot=(0,0,1;0rad)
  BaseFeature = -> Cylinder008
  FirstAngle = 0
  Height = 10
  MapMode = 5
  Placement = pos=(0,0,2) rot=(0,0,1;0rad)
  Radius = 1.75
  SecondAngle = 0
  Support = -> [XY_Plane019]
FEATURE [PartDesign::Body] Body003  label="White inset"
  Group = -> [Cylinder008,Cylinder009]
  Origin = -> Origin019
  Tip = -> Cylinder009
FEATURE [PartDesign::Fillet] Fillet002
  Base = -> Cylinder006 [Edge37]
  BaseFeature = -> Cylinder006
  Radius = 0.75
  SupportTransform = false
  UseAllEdges = false
FEATURE [PartDesign::SubtractiveCylinder] Cylinder007
  Angle = 360
  AttacherType = Attacher::AttachEngine3D
  AttachmentOffset = pos=(0,0,2) rot=(0,0,1;0rad)
  BaseFeature = -> Fillet002
  FirstAngle = 0
  Height = 10
  MapMode = 5
  Placement = pos=(0,0,2) rot=(0,0,1;0rad)
  Radius = 3.3
  SecondAngle = 0
  Support = -> [XY_Plane018]
FEATURE [PartDesign::Fillet] Fillet003
  Base = -> Cylinder007 [Edge19]
  BaseFeature = -> Cylinder007
  Placement = pos=(0,0,2) rot=(0,0,1;0rad)
  Radius = 0.2
  SupportTransform = false
  UseAllEdges = false
FEATURE [PartDesign::AdditiveBox] Box005
  AttacherType = Attacher::AttachEngine3D
  AttachmentOffset = pos=(-0.75,1.4,-10.1) rot=(0,0,1;0rad)
  BaseFeature = -> Fillet003
  Height = 10.1
  Length = 1.5
  MapMode = 5
  Placement = pos=(-0.75,1.4,-10.1) rot=(0,0,1;0rad)
  Support = -> [XY_Plane018]
  Width = 0.4
FEATURE [PartDesign::AdditiveBox] Box006
  AttacherType = Attacher::AttachEngine3D
  AttachmentOffset = pos=(4.95,-3,-3.4) rot=(0,0,1;0rad)
  BaseFeature = -> Box005
  Height = 3.8
  Length = 0.4
  MapMode = 5
  Placement = pos=(4.95,-3,-3.4) rot=(0,0,1;0rad)
  Support = -> [XY_Plane018]
  Width = 6
FEATURE [PartDesign::AdditiveBox] Box007
  AttacherType = Attacher::AttachEngine3D
  AttachmentOffset = pos=(-5.35,-3,-3.4) rot=(0,0,1;0rad)
  BaseFeature = -> Box006
  Height = 3.8
  Length = 0.4
  MapMode = 5
  Placement = pos=(-5.35,-3,-3.4) rot=(0,0,1;0rad)
  Support = -> [XY_Plane018]
  Width = 6
FEATURE [Sketcher::SketchObject] Sketch001  label="chassis-sketch001"
  FullyConstrained = false
  MapMode = 5
  Support = -> [XY_Plane018]
  sketch-geometry (36):
    g0: ArcOfCircle CenterX=0 CenterY=0 CenterZ=0 NormalX=0 NormalY=0 NormalZ=1 AngleXU=0 Radius=5.05 StartAngle=5.65934 EndAngle=6.28319
    g1: ArcOfCircle CenterX=0 CenterY=0 CenterZ=0 NormalX=0 NormalY=0 NormalZ=1 AngleXU=0 Radius=5.05 StartAngle=0 EndAngle=0.623843
    g2: ArcOfCircle CenterX=0 CenterY=0 CenterZ=0 NormalX=0 NormalY=0 NormalZ=1 AngleXU=0 Radius=5.05 StartAngle=0.648461 EndAngle=2.49313
    g3: ArcOfCircle CenterX=0 CenterY=0 CenterZ=0 NormalX=0 NormalY=0 NormalZ=1 AngleXU=0 Radius=5.05 StartAngle=2.51775 EndAngle=3.76544
    g4: ArcOfCircle CenterX=0 CenterY=0 CenterZ=0 NormalX=0 NormalY=0 NormalZ=1 AngleXU=0 Radius=5.05 StartAngle=3.79005 EndAngle=5.63472
    g5: ArcOfCircle CenterX=0 CenterY=0 CenterZ=0 NormalX=0 NormalY=0 NormalZ=1 AngleXU=0 Radius=4.95 StartAngle=5.6397 EndAngle=6.28319
    g6: ArcOfCircle CenterX=0 CenterY=0 CenterZ=0 NormalX=0 NormalY=0 NormalZ=1 AngleXU=0 Radius=4.95 StartAngle=0 EndAngle=0.643481
    g7: ArcOfCircle CenterX=0 CenterY=0 CenterZ=0 NormalX=0 NormalY=0 NormalZ=1 AngleXU=0 Radius=4.95 StartAngle=0.643521 EndAngle=2.49807
    g8: ArcOfCircle CenterX=0 CenterY=0 CenterZ=0 NormalX=0 NormalY=0 NormalZ=1 AngleXU=0 Radius=4.95 StartAngle=2.49811 EndAngle=3.78507
    g9: ArcOfCircle CenterX=0 CenterY=0 CenterZ=0 NormalX=0 NormalY=0 NormalZ=1 AngleXU=0 Radius=4.95 StartAngle=3.78511 EndAngle=5.63966
    g10: Circle CenterX=0 CenterY=0 CenterZ=0 NormalX=0 NormalY=0 NormalZ=1 AngleXU=0 Radius=1.3
    g11: Circle CenterX=0 CenterY=0 CenterZ=0 NormalX=0 NormalY=0 NormalZ=1 AngleXU=0 Radius=1.2
    g12: LineSegment StartX=-5.4 StartY=-3 StartZ=0 EndX=-5.4 EndY=3 EndZ=0
    g13: ArcOfCircle CenterX=-5.35 CenterY=3 CenterZ=0 NormalX=0 NormalY=0 NormalZ=1 AngleXU=-1e-16 Radius=0.05 StartAngle=0 EndAngle=3.14159
    g14: LineSegment StartX=-5.3 StartY=3 StartZ=0 EndX=-5.3 EndY=-3 EndZ=0
    g15: ArcOfCircle CenterX=-5.35 CenterY=-3 CenterZ=0 NormalX=0 NormalY=0 NormalZ=1 AngleXU=-1e-16 Radius=0.05 StartAngle=3.14159 EndAngle=6.28319
    g16: LineSegment StartX=5.3 StartY=-3 StartZ=0 EndX=5.3 EndY=3 EndZ=0
    g17: ArcOfCircle CenterX=5.35 CenterY=3 CenterZ=0 NormalX=0 NormalY=0 NormalZ=1 AngleXU=-1e-16 Radius=0.05 StartAngle=0 EndAngle=3.14159
    g18: LineSegment StartX=5.4 StartY=3 StartZ=0 EndX=5.4 EndY=-3 EndZ=0
    g19: ArcOfCircle CenterX=5.35 CenterY=-3 CenterZ=0 NormalX=0 NormalY=0 NormalZ=1 AngleXU=-1e-16 Radius=0.05 StartAngle=3.14159 EndAngle=6.28319
    g20: LineSegment StartX=-4 StartY=-3.05 StartZ=0 EndX=-5.35 EndY=-3.05 EndZ=0
    g21: ArcOfCircle CenterX=-5.35 CenterY=-3 CenterZ=0 NormalX=0 NormalY=0 NormalZ=1 AngleXU=1.5708 Radius=0.05 StartAngle=0 EndAngle=3.14159
    g22: LineSegment StartX=-5.35 StartY=-2.95 StartZ=0 EndX=-4 EndY=-2.95 EndZ=0
    g23: ArcOfCircle CenterX=-4 CenterY=-3 CenterZ=0 NormalX=0 NormalY=0 NormalZ=1 AngleXU=1.5708 Radius=0.05 StartAngle=3.14159 EndAngle=6.28319
    g24: LineSegment StartX=5.35 StartY=-3.05 StartZ=0 EndX=4 EndY=-3.05 EndZ=0
    g25: ArcOfCircle CenterX=4 CenterY=-3 CenterZ=0 NormalX=0 NormalY=0 NormalZ=1 AngleXU=1.5708 Radius=0.05 StartAngle=0 EndAngle=3.14159
    g26: LineSegment StartX=4 StartY=-2.95 StartZ=0 EndX=5.35 EndY=-2.95 EndZ=0
    g27: ArcOfCircle CenterX=5.35 CenterY=-3 CenterZ=0 NormalX=0 NormalY=0 NormalZ=1 AngleXU=1.5708 Radius=0.05 StartAngle=3.14159 EndAngle=6.28319
    g28: LineSegment StartX=5.35 StartY=2.95 StartZ=0 EndX=4 EndY=2.95 EndZ=0
    g29: ArcOfCircle CenterX=4 CenterY=3 CenterZ=0 NormalX=0 NormalY=0 NormalZ=1 AngleXU=1.5708 Radius=0.05 StartAngle=0 EndAngle=3.14159
    g30: LineSegment StartX=4 StartY=3.05 StartZ=0 EndX=5.35 EndY=3.05 EndZ=0
    g31: ArcOfCircle CenterX=5.35 CenterY=3 CenterZ=0 NormalX=0 NormalY=0 NormalZ=1 AngleXU=1.5708 Radius=0.05 StartAngle=3.14159 EndAngle=6.28319
    g32: LineSegment StartX=-4 StartY=2.95 StartZ=0 EndX=-5.35 EndY=2.95 EndZ=0
    g33: ArcOfCircle CenterX=-5.35 CenterY=3 CenterZ=0 NormalX=0 NormalY=0 NormalZ=1 AngleXU=1.5708 Radius=0.05 StartAngle=0 EndAngle=3.14159
    g34: LineSegment StartX=-5.35 StartY=3.05 StartZ=0 EndX=-4 EndY=3.05 EndZ=0
    g35: ArcOfCircle CenterX=-4 CenterY=3 CenterZ=0 NormalX=0 NormalY=0 NormalZ=1 AngleXU=1.5708 Radius=0.05 StartAngle=3.14159 EndAngle=6.28319
FEATURE [PartDesign::Body] Body002
  Group = -> [Sketch001,Box004,Cylinder005,Cylinder006,Fillet002,Cylinder007,Fillet003,Box005,Box006,Box007]
  Origin = -> Origin018
  Tip = -> Box007
FEATURE [App::Part] Part001  label="RCA-White"
  Group = -> [Body002,Body003]
  Origin = -> Origin020
  Placement = pos=(21.65,11.95,4) rot=(0,0,1;2.79253rad)
FEATURE [App::Part] Top_ecc4
  Group = -> [Shape,Shape001,R12_R_0603_1608Metric_fea975d0d3e0_ln_,Norcomp_111_014_213L001,J5_PinHeader_1x04_P254mm_Horizontal_92fba9bb2b89_ln_,R12_R_0603_1608Metric_fea975d0d3e0_ln_001,TC_1578891_scart,Shape002,R12_R_0603_1608Metric_fea975d0d3e0_ln_002,Part,Part001]
  Origin = -> Origin003
FEATURE [App::Part] Step_Models_ecc4
  Group = -> [Top_ecc4,Bot_ecc4]
  Origin = -> Origin002
FEATURE [App::Part] Board_ecc4  label="ultra-AV"
  Group = -> [Board_Geoms_ecc4,Step_Models_ecc4]
  Origin = -> Origin001
